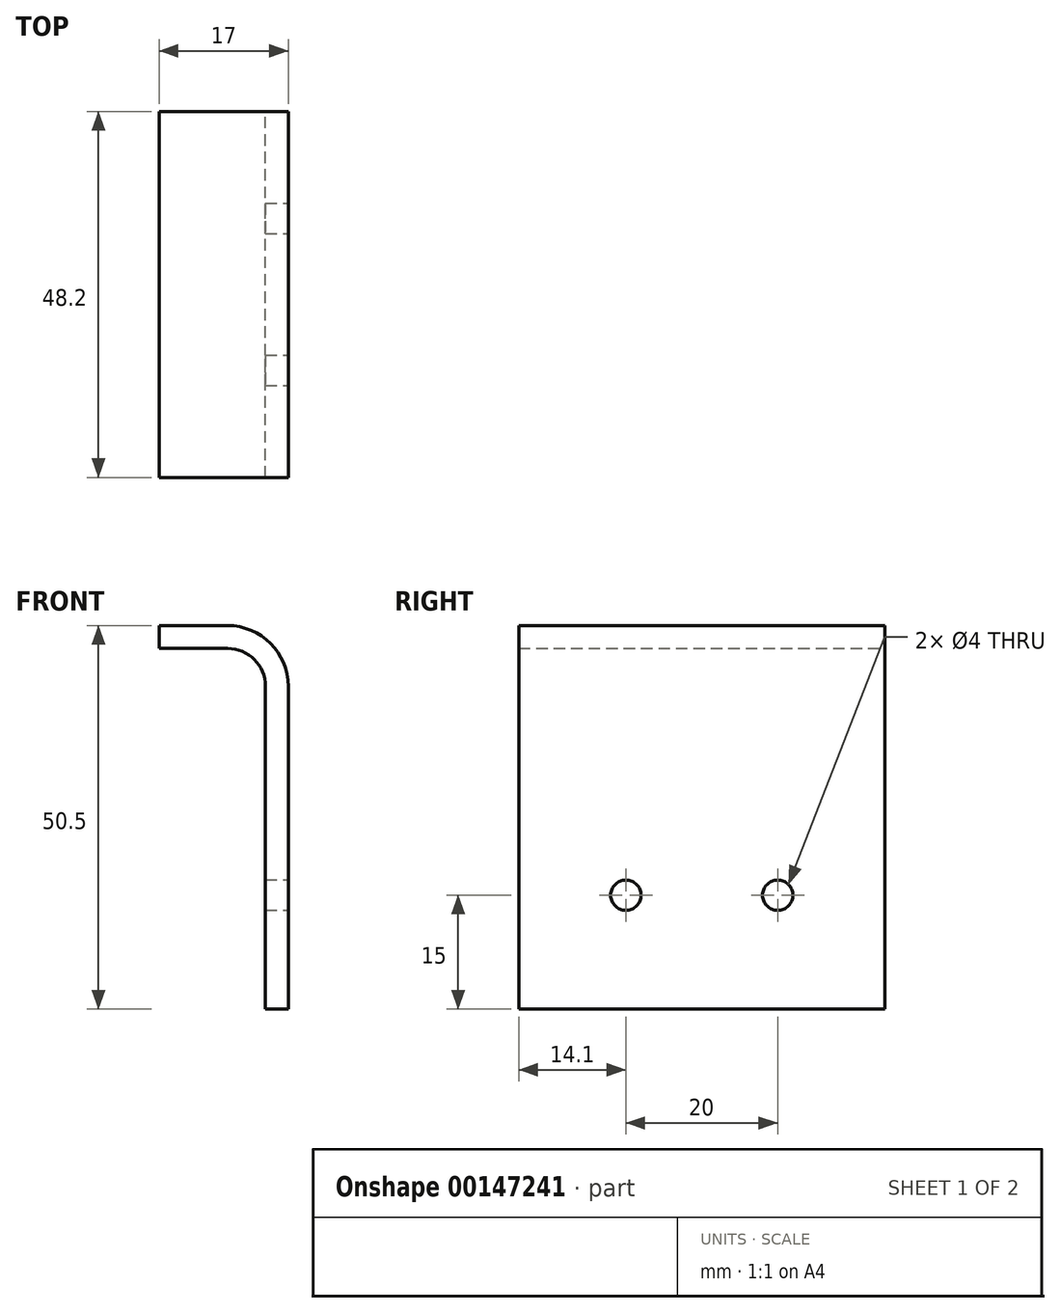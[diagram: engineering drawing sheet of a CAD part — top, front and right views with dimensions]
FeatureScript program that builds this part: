
annotation { "Feature Type Name" : "Feature", "Feature Type Description" : "" }
export const myFeature = defineFeature(function(context is Context, id is Id, definition is map)
    precondition{}
    {
        {
            var Q0;
            Q0=qCreatedBy(makeId("Front.planeOp"),FACE);
            var sketch = newSketch(context, id + "F0", { "sketchPlane" : qUnion([Q0])});
            skLineSegment(sketch, "E0", {"start": v(0, 0) * mm, "end": v(3, 0) * mm});
            skLineSegment(sketch, "E1", {"start": v(3, 0) * mm, "end": v(3, 42.5) * mm});
            skLineSegment(sketch, "E2", {"start": v(-5, 50.5) * mm, "end": v(-14, 50.5) * mm});
            skLineSegment(sketch, "E3", {"start": v(-14, 50.5) * mm, "end": v(-14, 47.5) * mm});
            skLineSegment(sketch, "E4", {"start": v(-14, 47.5) * mm, "end": v(-5, 47.5) * mm});
            skLineSegment(sketch, "E5", {"start": v(0, 42.5) * mm, "end": v(0, 0) * mm});
            skPoint(sketch, "E6.visualSharp", {"position": v(0, 47.5) * mm});
            skArc(sketch, "E6.filletArc", {"start": v(0, 42.5) * mm, "mid": v(-1.46, 46.04) * mm, "end": v(-5, 47.5) * mm});
            skPoint(sketch, "E7.visualSharp", {"position": v(3, 50.5) * mm});
            skArc(sketch, "E7.filletArc", {"start": v(3, 42.5) * mm, "mid": v(0.66, 48.16) * mm, "end": v(-5, 50.5) * mm});
            skSolve(sketch);
        }
        {
            var Q0;
            Q0 = qSketchRegion(id + "F0", true);
            extrude(context, id + "F1", {"entities" : qUnion([Q0]), "endBound" : BoundingType.SYMMETRIC, "depth" : 48.2 * mm});
        }
        {
            var Q0;
            Q0=makeQuery(id+"F1.opExtrude","SWEPT_FACE",FACE,{"disambiguationData":[OSD([sQuery(id+"F0.wireOp",EDGE,"E1")])]});
            var sketch = newSketch(context, id + "F2", { "sketchPlane" : qUnion([Q0])});
            skCircle(sketch, "E8", {"center": v(-10, 15) * mm, "radius": 2 * mm});
            skCircle(sketch, "E9", {"center": v(10, 15) * mm, "radius": 2 * mm});
            skLineSegment(sketch, "E10", {"start": v(-10, 15) * mm, "end": v(10, 15) * mm, "construction": true});
            skLineSegment(sketch, "E11", {"start": v(0, 0) * mm, "end": v(0, 15) * mm, "construction": true});
            skSolve(sketch);
        }
        {
            var Q0;
            Q0 = qSketchRegion(id + "F2", true);
            extrude(context, id + "F3", {"entities" : qUnion([Q0]), "operationType" : NewBodyOperationType.REMOVE, "endBound" : BoundingType.THROUGH_ALL, "oppositeDirection" : true, "depth" : 25 * mm});
        }
    });
